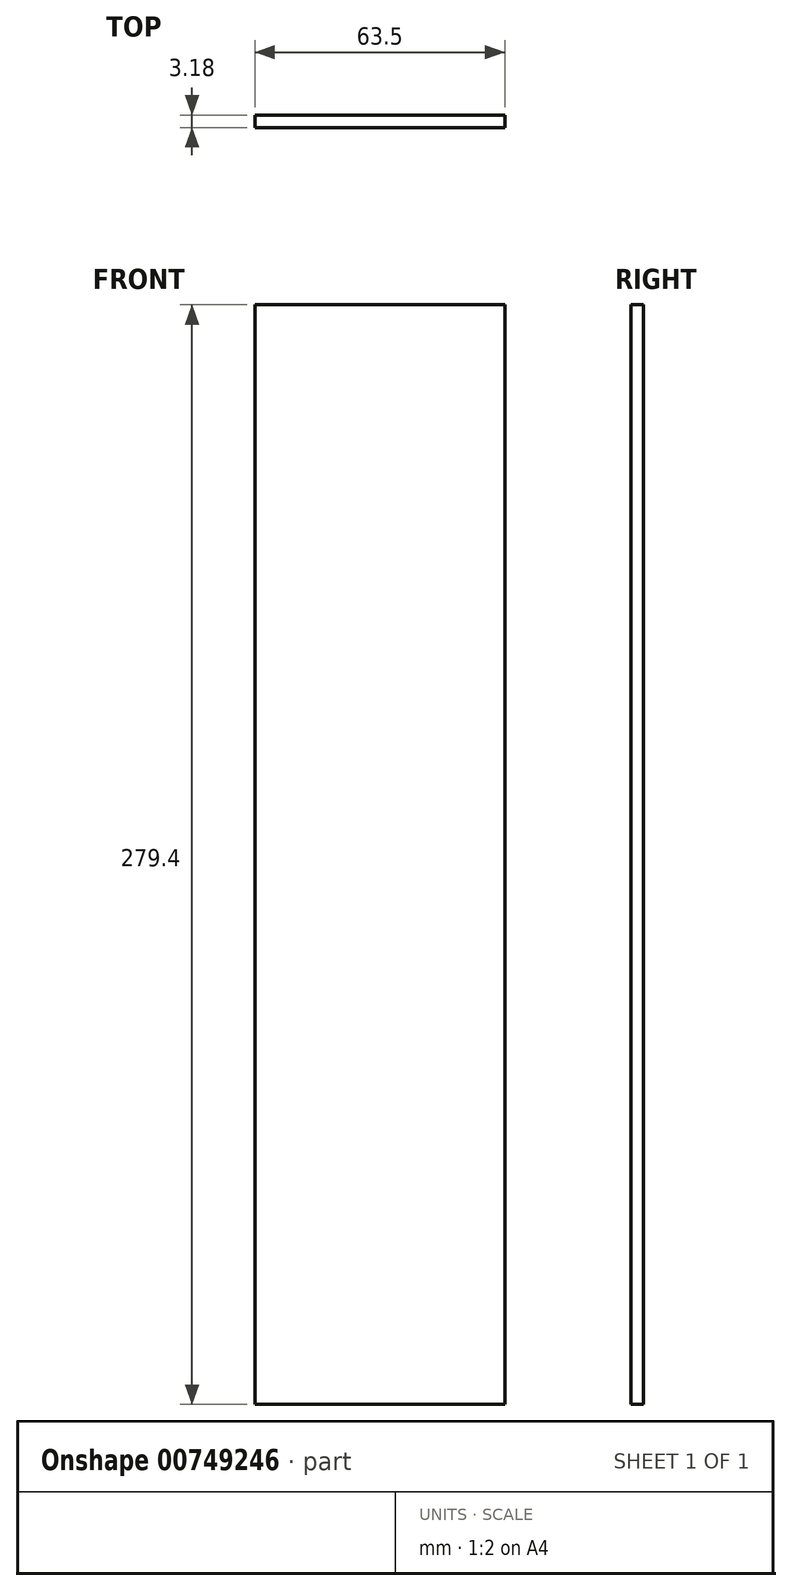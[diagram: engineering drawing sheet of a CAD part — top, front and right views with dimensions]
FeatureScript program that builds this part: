
annotation { "Feature Type Name" : "Feature", "Feature Type Description" : "" }
export const myFeature = defineFeature(function(context is Context, id is Id, definition is map)
    precondition{}
    {
        {
            var Q0;
            Q0=qCreatedBy(makeId("Top.planeOp"),FACE);
            var sketch = newSketch(context, id + "F0", { "sketchPlane" : qUnion([Q0])});
            skLineSegment(sketch, "E0.bottom", {"start": v(31.75, 1.59) * mm, "end": v(-31.75, 1.59) * mm});
            skLineSegment(sketch, "E0.top", {"start": v(31.75, -1.59) * mm, "end": v(-31.75, -1.59) * mm});
            skLineSegment(sketch, "E0.left", {"start": v(31.75, 1.59) * mm, "end": v(31.75, -1.59) * mm});
            skLineSegment(sketch, "E0.right", {"start": v(-31.75, 1.59) * mm, "end": v(-31.75, -1.59) * mm});
            skPoint(sketch, "E0.middle", {"position": v(0, 0) * mm});
            skSolve(sketch);
        }
        {
            var Q0;
            Q0 = qSketchRegion(id + "F0", true);
            extrude(context, id + "F1", {"entities" : qUnion([Q0]), "depth" : 279.4 * mm, "offsetDistance" : 25.4 * mm});
        }
    });
